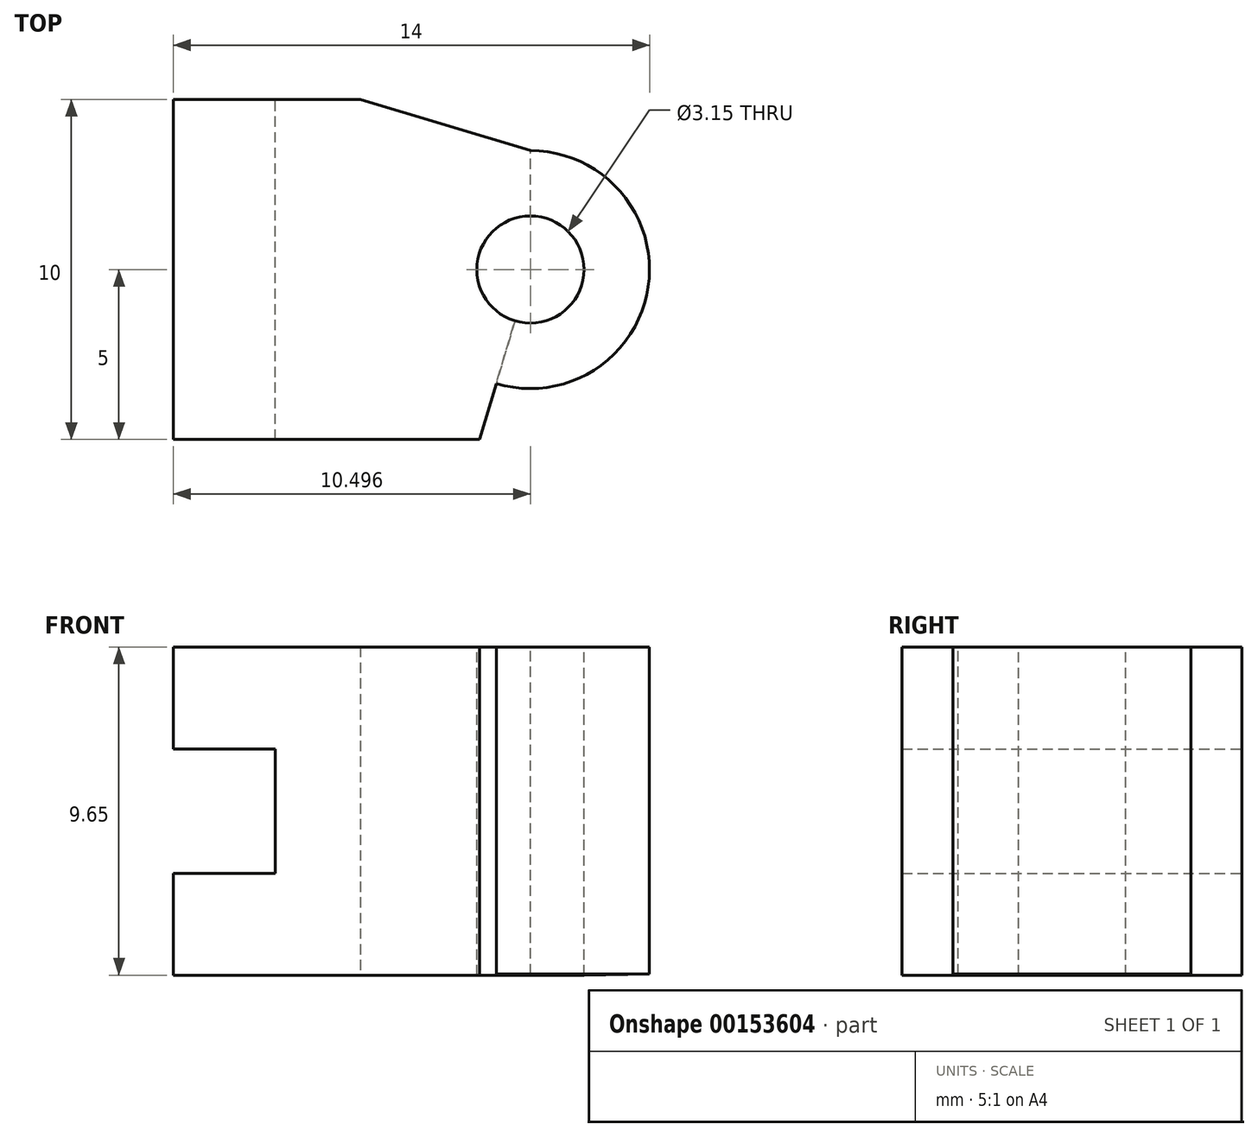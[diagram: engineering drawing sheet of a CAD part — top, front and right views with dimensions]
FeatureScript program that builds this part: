
annotation { "Feature Type Name" : "Feature", "Feature Type Description" : "" }
export const myFeature = defineFeature(function(context is Context, id is Id, definition is map)
    precondition{}
    {
        {
            var Q0;
            Q0=qCreatedBy(makeId("Front.planeOp"),FACE);
            var sketch = newSketch(context, id + "F0", { "sketchPlane" : qUnion([Q0])});
            skLineSegment(sketch, "E0", {"start": v(-4.7, -4.2) * mm, "end": v(1.8, -4.2) * mm});
            skLineSegment(sketch, "E1", {"start": v(1.8, -4.2) * mm, "end": v(1.8, 5.46) * mm});
            skLineSegment(sketch, "E2", {"start": v(1.8, 5.46) * mm, "end": v(-4.7, 5.46) * mm});
            skLineSegment(sketch, "E3", {"start": v(-4.7, 5.46) * mm, "end": v(-4.7, 2.46) * mm});
            skLineSegment(sketch, "E4", {"start": v(-4.7, 2.46) * mm, "end": v(-1.7, 2.46) * mm});
            skLineSegment(sketch, "E5", {"start": v(-1.7, 2.46) * mm, "end": v(-1.7, -1.2) * mm});
            skLineSegment(sketch, "E6", {"start": v(-1.7, -1.2) * mm, "end": v(-4.7, -1.2) * mm});
            skLineSegment(sketch, "E7", {"start": v(-4.7, -1.2) * mm, "end": v(-4.7, -4.2) * mm});
            skLineSegment(sketch, "E8", {"start": v(1.8, 5.46) * mm, "end": v(5.8, 5.46) * mm});
            skLineSegment(sketch, "E9", {"start": v(5.8, 5.46) * mm, "end": v(5.8, -4.2) * mm});
            skLineSegment(sketch, "E10", {"start": v(5.8, -4.2) * mm, "end": v(1.8, -4.2) * mm});
            skLineSegment(sketch, "E11", {"start": v(5.8, 5.46) * mm, "end": v(7.38, 5.46) * mm});
            skLineSegment(sketch, "E12", {"start": v(7.38, 5.46) * mm, "end": v(7.38, -4.2) * mm});
            skLineSegment(sketch, "E13", {"start": v(7.38, -4.2) * mm, "end": v(5.8, -4.2) * mm});
            skLineSegment(sketch, "E14", {"start": v(5.8, 5.46) * mm, "end": v(9.3, 5.46) * mm});
            skLineSegment(sketch, "E15", {"start": v(9.3, 5.46) * mm, "end": v(9.3, -4.16) * mm});
            skLineSegment(sketch, "E16", {"start": v(9.3, -4.16) * mm, "end": v(7.38, -4.2) * mm});
            skSolve(sketch);
        }
        {
            var Q0;
            Q0=makeQuery(id+"F0.imprint","IMPRINT",FACE,{"disambiguationData":[TD([[makeQuery(id+"F0.imprint","IMPRINT",EDGE,{"derivedFrom":sQuery(id+"F0.wireOp",EDGE,"E0")}),1.0]])]});
            extrude(context, id + "F1", {"entities" : qUnion([Q0]), "depth" : 10 * mm, "symmetric" : true});
        }
        {
            var Q0;
            Q0=makeQuery(id+"F0.imprint","IMPRINT",FACE,{"disambiguationData":[TD([[makeQuery(id+"F0.imprint","IMPRINT",EDGE,{"derivedFrom":sQuery(id+"F0.wireOp",EDGE,"E1")}),-1.0]])]});
            extrude(context, id + "F2", {"entities" : qUnion([Q0]), "operationType" : NewBodyOperationType.ADD, "depth" : 10 * mm, "symmetric" : true});
        }
        {
            var Q0;
            Q0=makeQuery(id+"F2.opExtrude","CAP_EDGE",EDGE,{"disambiguationData":[OSD([sQuery(id+"F0.wireOp",EDGE,"E9")])],"isStart":false});
            chamfer(context, id + "F3", {"entities" : qUnion([Q0]), "chamferType" : ChamferType.TWO_OFFSETS, "width1" : 1.5 * mm, "oppositeDirection" : false, "width2" : 5 * mm, "tangentPropagation" : true});
        }
        {
            var Q0;
            Q0=makeQuery(id+"F2.opExtrude","CAP_EDGE",EDGE,{"disambiguationData":[OSD([sQuery(id+"F0.wireOp",EDGE,"E9")])],"isStart":true});
            chamfer(context, id + "F4", {"entities" : qUnion([Q0]), "chamferType" : ChamferType.TWO_OFFSETS, "width1" : 5 * mm, "oppositeDirection" : false, "width2" : 1.5 * mm, "tangentPropagation" : true});
        }
        {
            var Q0;
            Q0=makeQuery(id+"F0.imprint","IMPRINT",FACE,{"disambiguationData":[TD([[makeQuery(id+"F0.imprint","IMPRINT",EDGE,{"derivedFrom":sQuery(id+"F0.wireOp",EDGE,"E9")}),1.0]])]});
            var Q1;
            Q1=sQuery(id+"F0.wireOp",EDGE,"E9");
            revolve(context, id + "F5", {"operationType" : NewBodyOperationType.REMOVE, "entities" : qUnion([Q0]), "axis" : qUnion([Q1]), "revolveType" : RevolveType.FULL});
        }
        {
            var Q0;
            {var subQ0=sQuery(id+"F0.wireOp",EDGE,"E12");Q0=makeQuery(id+"F0.imprint","IMPRINT",FACE,{"disambiguationData":[TD([[makeQuery(id+"F0.imprint","IMPRINT",EDGE,{"derivedFrom":subQ0}),1.0]])]});}
            var Q1;
            Q1=sQuery(id+"F0.wireOp",EDGE,"E9");
            revolve(context, id + "F6", {"operationType" : NewBodyOperationType.ADD, "entities" : qUnion([Q0]), "axis" : qUnion([Q1]), "revolveType" : RevolveType.FULL});
        }
    });
